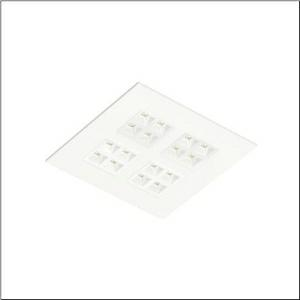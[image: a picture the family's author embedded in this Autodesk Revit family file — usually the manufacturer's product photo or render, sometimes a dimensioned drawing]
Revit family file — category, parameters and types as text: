
# Revit family: silica_31_square_51my6nmu44wa
name_source: partatom
category: Lighting Fixtures
units: mm (PartAtom-declared; Revit-internal decimal feet)

## family parameters
Cut with Voids When Loaded = No
Host = Face
Light Source = No
Part Type = Normal
Room Calculation Point = No
Round Connector Dimension = Use Diameter
Shared = No

## types (1)
- --- (1 x LED, 6970 lm, 39 W, 4000K)
    Apparent Load = 39 VA
    CIE Flux Codes = 81 99 100 100 100
    Color Rendering = 80
    Color Temperature = 4000K
    Default Elevation = 1800 mm
    Description = Silica 31 Square, office luminaire, primary light control with lens, of PMMA, primary anti-glare with reflector, of PC, white, light emission: direct distribution, primary light characteristic: symmetric, installation type: lay-in mounting, LED, rated luminous flux: 4.560lm, luminous efficacy: 186lm/W, light colour: 840, colour temperature: 4000K, control gear: ON/OFF Multilumen, with terminal, 3-pole, mains connection: 220..240V, AC, 50/60Hz, rated input power: 24.5W, luminaire housing, of sheet steel, coated, traffic white (RAL 9016), module: M625, length: 620mm, width: 620mm, height: 43mm, protection rating (complete): IP20, insulation class (complete): insulation class II (safety insulation), certification: CE, impact resistance: IK03, permissible operating ambient temperature: -20..+35°C, standard: EN 50419, packaging unit: 1 piece
    Height = 0 mm  [stored 0 ft]
    Lamp = 1 x LED
    Lamp Light Flux = 6970 lm
    Lamp Power = 39 W
    Lamp count = 1
    Length = 620 mm
    Luminous efficacy = 179 lm/W
    Manufacturer = Siteco
    ModVariant = No
    Model = 51MY6NMU44WA
    Mounting Place = Ceiling
    Mounting Type = Recessed
    Number of Poles = 1
    OnlyDefault = Yes
    Power Factor = 1
    Product Name = Silica 31 Square
    Product group = office luminaire | ceiling recessed
    ProductGroupID = 400
    Protection Class = Protection class II
    Protection Degree = IP 20
    RLX_Detail_Level = 1
    RLX_Emergency_Light_Flux = 0 lm
    RLX_Emergency_Type = 0
    RLX_Emergency_Type_DB = No
    RlxData = <blob elided: 28933 chars, md5=b3dbb0e0>
    Socket = socket
    Standby Power = 0 W
    System Light Flux = 6970 lm
    System Power = 39 W
    Type Comments = factory setting: luminous flux: 100 % | (ON | ON | ON | ON) | 1100 mA
    Type Image = l_1313651.jpg
    URL = http://relux.com
    VarID = @adj_043157
    Voltage = 0 V
    Weight = 0.00 kg
    Width = 620 mm

note: [stored X ft] marks values corroborated as IEEE doubles in the binary element streams (Revit-internal decimal feet)

## geometry (parser evidence)
native form markers: Blend x4, Sweep x9
no freeform markers — native parametric forms only
